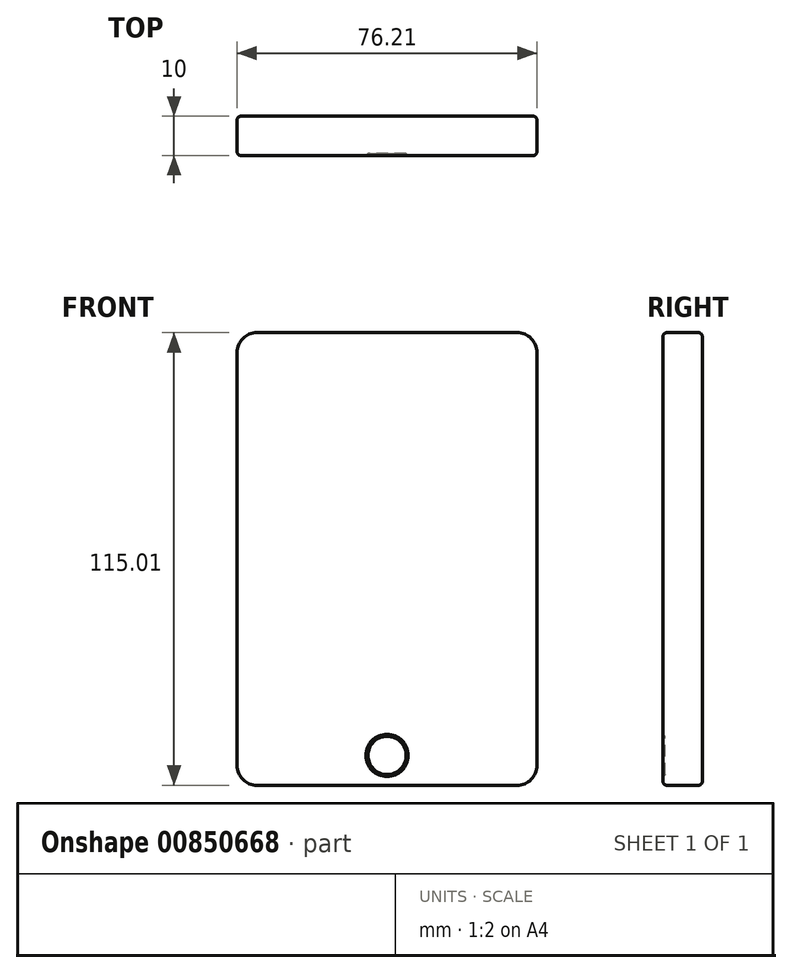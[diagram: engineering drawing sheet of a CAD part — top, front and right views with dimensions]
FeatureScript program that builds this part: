
annotation { "Feature Type Name" : "Feature", "Feature Type Description" : "" }
export const myFeature = defineFeature(function(context is Context, id is Id, definition is map)
    precondition{}
    {
        {
            var Q0;
            Q0=qCreatedBy(makeId("Front.planeOp"),FACE);
            var sketch = newSketch(context, id + "F0", { "sketchPlane" : qUnion([Q0])});
            skLineSegment(sketch, "E0.bottom", {"start": v(-71.13, 62.34) * mm, "end": v(-5.08, 62.34) * mm});
            skLineSegment(sketch, "E0.top", {"start": v(-71.13, -52.67) * mm, "end": v(-5.08, -52.67) * mm});
            skLineSegment(sketch, "E0.left", {"start": v(-76.21, 57.26) * mm, "end": v(-76.21, -47.6) * mm});
            skLineSegment(sketch, "E0.right", {"start": v(0, 57.26) * mm, "end": v(0, -47.6) * mm});
            skPoint(sketch, "E1.visualSharp", {"position": v(-76.21, 62.34) * mm});
            skArc(sketch, "E1.filletArc", {"start": v(-71.13, 62.34) * mm, "mid": v(-74.73, 60.85) * mm, "end": v(-76.21, 57.26) * mm});
            skPoint(sketch, "E2.visualSharp", {"position": v(0, 62.34) * mm});
            skArc(sketch, "E2.filletArc", {"start": v(0, 57.26) * mm, "mid": v(-1.49, 60.85) * mm, "end": v(-5.08, 62.34) * mm});
            skPoint(sketch, "E3.visualSharp", {"position": v(0, -52.67) * mm});
            skArc(sketch, "E3.filletArc", {"start": v(-5.08, -52.67) * mm, "mid": v(-1.49, -51.18) * mm, "end": v(0, -47.6) * mm});
            skPoint(sketch, "E4.visualSharp", {"position": v(-76.21, -52.67) * mm});
            skArc(sketch, "E4.filletArc", {"start": v(-76.21, -47.6) * mm, "mid": v(-74.73, -51.18) * mm, "end": v(-71.13, -52.67) * mm});
            skLineSegment(sketch, "E5.0", {"start": v(-66.05, 47.1) * mm, "end": v(-10.16, 47.1) * mm});
            skLineSegment(sketch, "E6.0", {"start": v(-66.05, -37.43) * mm, "end": v(-10.16, -37.43) * mm});
            skLineSegment(sketch, "E7", {"start": v(-68.6, 44.56) * mm, "end": v(-68.6, -34.9) * mm});
            skLineSegment(sketch, "E8", {"start": v(-7.62, 44.56) * mm, "end": v(-7.62, -34.9) * mm});
            skPoint(sketch, "E9.visualSharp", {"position": v(-68.6, 47.1) * mm});
            skArc(sketch, "E9.filletArc", {"start": v(-66.05, 47.1) * mm, "mid": v(-67.85, 46.36) * mm, "end": v(-68.6, 44.56) * mm});
            skPoint(sketch, "E10.visualSharp", {"position": v(-7.62, 47.1) * mm});
            skArc(sketch, "E10.filletArc", {"start": v(-7.62, 44.56) * mm, "mid": v(-8.36, 46.36) * mm, "end": v(-10.16, 47.1) * mm});
            skPoint(sketch, "E11.visualSharp", {"position": v(-7.62, -37.43) * mm});
            skArc(sketch, "E11.filletArc", {"start": v(-10.16, -37.43) * mm, "mid": v(-8.36, -36.69) * mm, "end": v(-7.62, -34.9) * mm});
            skPoint(sketch, "E12.visualSharp", {"position": v(-68.6, -37.43) * mm});
            skArc(sketch, "E12.filletArc", {"start": v(-68.6, -34.9) * mm, "mid": v(-67.85, -36.69) * mm, "end": v(-66.05, -37.43) * mm});
            skCircle(sketch, "E13", {"center": v(-38.1, -45.08) * mm, "radius": 4.86 * mm});
            skPoint(sketch, "E13.centerSnap0", {"position": v(-38.1, -37.43) * mm});
            skCircle(sketch, "E14", {"center": v(-38.1, -45.08) * mm, "radius": 5.5 * mm});
            skSolve(sketch);
        }
        {
            var Q0;
            Q0=makeQuery(id+"F0.imprint","IMPRINT",FACE,{"disambiguationData":[TD([[makeQuery(id+"F0.imprint","IMPRINT",EDGE,{"derivedFrom":sQuery(id+"F0.wireOp",EDGE,"E5.0")}),-1.0]])]});
            var Q1;
            Q1=makeQuery(id+"F0.imprint","IMPRINT",FACE,{"disambiguationData":[TD([[makeQuery(id+"F0.imprint","IMPRINT",EDGE,{"derivedFrom":sQuery(id+"F0.wireOp",EDGE,"E0.bottom")}),-1.0]])]});
            extrude(context, id + "F1", {"entities" : qUnion([Q0, Q1]), "depth" : 10 * mm, "offsetDistance" : 25.4 * mm});
        }
        {
            var Q0;
            Q0=makeQuery(id+"F0.imprint","IMPRINT",FACE,{"disambiguationData":[TD([[makeQuery(id+"F0.imprint","IMPRINT",EDGE,{"derivedFrom":sQuery(id+"F0.wireOp",EDGE,"E13")}),-1.0]])]});
            extrude(context, id + "F2", {"entities" : qUnion([Q0]), "operationType" : NewBodyOperationType.ADD, "depth" : 10 * mm, "offsetDistance" : 25.4 * mm});
        }
        {
            var Q0;
            Q0=makeQuery(id+"F2.opExtrude","CAP_EDGE",EDGE,{"disambiguationData":[OSD([sQuery(id+"F0.wireOp",EDGE,"E13")])],"isStart":false});
            chamfer(context, id + "F3", {"entities" : qUnion([Q0]), "width" : 0.5 * mm, "tangentPropagation" : true});
        }
        {
            var Q0;
            Q0=makeQuery(id+"F0.imprint","IMPRINT",FACE,{"disambiguationData":[TD([[makeQuery(id+"F0.imprint","IMPRINT",EDGE,{"derivedFrom":sQuery(id+"F0.wireOp",EDGE,"E13")}),1.0]])]});
            extrude(context, id + "F4", {"entities" : qUnion([Q0]), "operationType" : NewBodyOperationType.ADD, "depth" : 9.5 * mm, "offsetDistance" : 25.4 * mm});
        }
        {
            var Q0;
            Q0=makeQuery(id+"F1.opExtrude","CAP_EDGE",EDGE,{"disambiguationData":[OSD([sQuery(id+"F0.wireOp",EDGE,"E0.left")])],"isStart":false});
            var Q1;
            Q1=makeQuery(id+"F1.opExtrude","CAP_EDGE",EDGE,{"disambiguationData":[OSD([sQuery(id+"F0.wireOp",EDGE,"E1.filletArc")])],"isStart":true});
            var Q2;
            Q2=makeQuery(id+"F1.opExtrude","SWEPT_FACE",FACE,{"disambiguationData":[OSD([sQuery(id+"F0.wireOp",EDGE,"E0.left")])]});
            var Q3;
            Q3=makeQuery(id+"F1.opExtrude","SWEPT_EDGE",EDGE,{"disambiguationData":[OSD([sQuery(id+"F0.wireOp",EDGE,"E0.bottom"),sQuery(id+"F0.wireOp",EDGE,"E1.filletArc")])]});
            var Q4;
            Q4=makeQuery(id+"F1.opExtrude","SWEPT_EDGE",EDGE,{"disambiguationData":[OSD([sQuery(id+"F0.wireOp",EDGE,"E0.left"),sQuery(id+"F0.wireOp",EDGE,"E1.filletArc")])]});
            var Q5;
            Q5=makeQuery(id+"F1.opExtrude","SWEPT_EDGE",EDGE,{"disambiguationData":[OSD([sQuery(id+"F0.wireOp",EDGE,"E0.top"),sQuery(id+"F0.wireOp",EDGE,"E4.filletArc")])]});
            var Q6;
            Q6=makeQuery(id+"F1.opExtrude","CAP_EDGE",EDGE,{"disambiguationData":[OSD([sQuery(id+"F0.wireOp",EDGE,"E4.filletArc")])],"isStart":true});
            var Q7;
            Q7=makeQuery(id+"F1.opExtrude","SWEPT_EDGE",EDGE,{"disambiguationData":[OSD([sQuery(id+"F0.wireOp",EDGE,"E0.left"),sQuery(id+"F0.wireOp",EDGE,"E4.filletArc")])]});
            var Q8;
            Q8=makeQuery(id+"F1.opExtrude","CAP_EDGE",EDGE,{"disambiguationData":[OSD([sQuery(id+"F0.wireOp",EDGE,"E0.top")])],"isStart":true});
            var Q9;
            Q9=makeQuery(id+"F1.opExtrude","CAP_EDGE",EDGE,{"disambiguationData":[OSD([sQuery(id+"F0.wireOp",EDGE,"E0.top")])],"isStart":false});
            var Q10;
            Q10=makeQuery(id+"F1.opExtrude","SWEPT_EDGE",EDGE,{"disambiguationData":[OSD([sQuery(id+"F0.wireOp",EDGE,"E0.right"),sQuery(id+"F0.wireOp",EDGE,"E3.filletArc")])]});
            var Q11;
            Q11=makeQuery(id+"F1.opExtrude","SWEPT_EDGE",EDGE,{"disambiguationData":[OSD([sQuery(id+"F0.wireOp",EDGE,"E0.top"),sQuery(id+"F0.wireOp",EDGE,"E3.filletArc")])]});
            var Q12;
            Q12=makeQuery(id+"F1.opExtrude","CAP_EDGE",EDGE,{"disambiguationData":[OSD([sQuery(id+"F0.wireOp",EDGE,"E0.right")])],"isStart":false});
            var Q13;
            Q13=makeQuery(id+"F1.opExtrude","CAP_EDGE",EDGE,{"disambiguationData":[OSD([sQuery(id+"F0.wireOp",EDGE,"E0.right")])],"isStart":true});
            fillet(context, id + "F5", {"entities" : qUnion([Q0, Q1, Q2, Q3, Q4, Q5, Q6, Q7, Q8, Q9, Q10, Q11, Q12, Q13]), "radius" : 1 * mm, "tangentPropagation" : true, "allowEdgeOverflow" : false});
        }
    });
